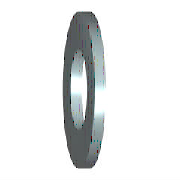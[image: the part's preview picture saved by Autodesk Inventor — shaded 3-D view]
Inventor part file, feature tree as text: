
AUTODESK INVENTOR PART (.ipt)
format: ipt  version: 2015 (Build 190159000, 159)  size: 105,984 bytes
history: native  units: mm (DEFAULTED — no unit token found)
features: other x1, plane x1, sketch x1
ambient origin geometry x7: Origin, YZ Plane, XY Plane, X Axis, Y Axis, Z Axis, Center Point
bodies: Solid1 (feature_tree), Body (feature_tree)
feature tree (3):
  other  "Work Axis1"
  plane  "Work Plane1"
  sketch  "Sketch"  dims[d0=8.4mm d1=24.0mm d2=2.0mm d3=0.0mm d4=0.0mm d5=0.0mm d6=0.0mm d7=0.0mm]
